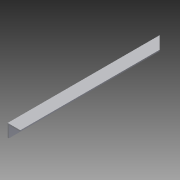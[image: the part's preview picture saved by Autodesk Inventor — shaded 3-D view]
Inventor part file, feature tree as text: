
AUTODESK INVENTOR PART (.ipt)
format: ipt  version: 2014 (Build 180170000, 170)  size: 81,920 bytes
history: native  units: in
note: dims shown in document units (in); Inventor stores cm internally (conversion verified against a paired STEP export)
features: extrude x2, sketch x2
ambient origin geometry x8: Origin, YZ Plane, XZ Plane, XY Plane, X Axis, Y Axis, Z Axis, Center Point
bodies: Solid1 (feature_tree)
feature tree (4):
  extrude  "Extrusion1"  Depth=0.5in
  extrude  "Extrusion2"  Depth=0.45in
  sketch  "Sketch1"  dims[d0=0.5in d1=0.5in]
  sketch  "Sketch2"  dims[d2=0.05in d3=0.45in d4=6.0in d5=0.0in d6=45.0deg d8=9.0in d9=0.0in]
